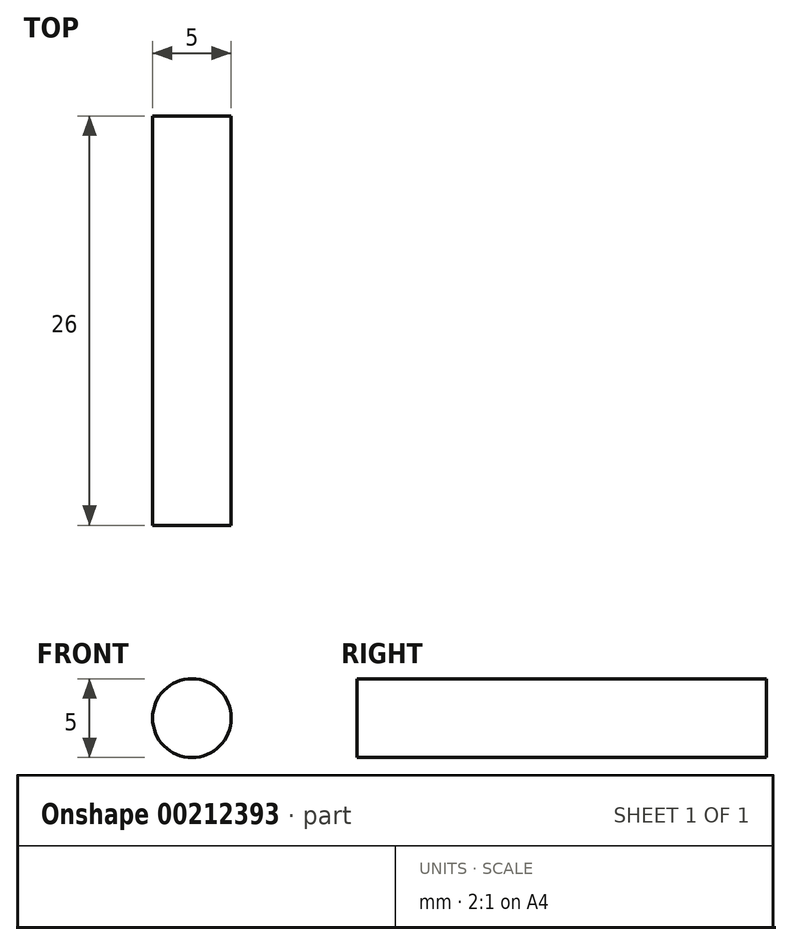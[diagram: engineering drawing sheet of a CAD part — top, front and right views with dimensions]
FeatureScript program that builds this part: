
annotation { "Feature Type Name" : "Feature", "Feature Type Description" : "" }
export const myFeature = defineFeature(function(context is Context, id is Id, definition is map)
    precondition{}
    {
        {
            var Q0;
            Q0=qCreatedBy(makeId("Front.planeOp"),FACE);
            var sketch = newSketch(context, id + "F0", { "sketchPlane" : qUnion([Q0])});
            skCircle(sketch, "E0", {"center": v(0, 0) * mm, "radius": 2.5 * mm});
            skSolve(sketch);
        }
        {
            var Q0;
            Q0=makeQuery(id+"F0.imprint","IMPRINT",FACE,{"disambiguationData":[TD([[makeQuery(id+"F0.imprint","IMPRINT",EDGE,{"derivedFrom":sQuery(id+"F0.wireOp",EDGE,"E0")}),1.0]])]});
            extrude(context, id + "F1", {"entities" : qUnion([Q0]), "depth" : 26 * mm});
        }
    });
